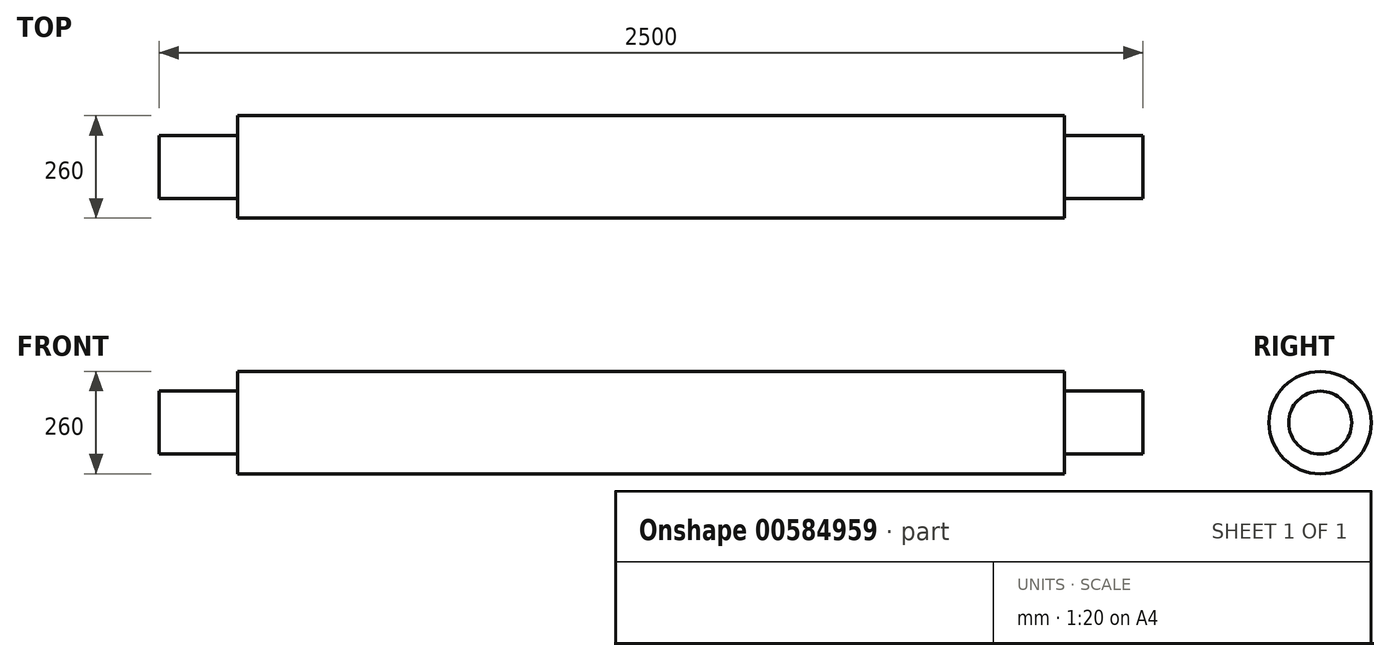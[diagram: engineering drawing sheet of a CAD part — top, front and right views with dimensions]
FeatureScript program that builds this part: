
annotation { "Feature Type Name" : "Feature", "Feature Type Description" : "" }
export const myFeature = defineFeature(function(context is Context, id is Id, definition is map)
    precondition{}
    {
        {
            var Q0;
            Q0=qCreatedBy(makeId("Front.planeOp"),FACE);
            var sketch = newSketch(context, id + "F0", { "sketchPlane" : qUnion([Q0])});
            skLineSegment(sketch, "E0", {"start": v(-1250, 0) * mm, "end": v(1250, 0) * mm});
            skLineSegment(sketch, "E1", {"start": v(0, 130) * mm, "end": v(0, 0) * mm, "construction": true});
            skLineSegment(sketch, "E2", {"start": v(0, 0) * mm, "end": v(0, 0) * mm});
            skLineSegment(sketch, "E3", {"start": v(-1250, 0) * mm, "end": v(-1250, 80) * mm});
            skLineSegment(sketch, "E4", {"start": v(-1250, 80) * mm, "end": v(-1050, 80) * mm});
            skLineSegment(sketch, "E5", {"start": v(-1050, 80) * mm, "end": v(-1050, 130) * mm});
            skLineSegment(sketch, "E6", {"start": v(-1050, 130) * mm, "end": v(0, 130) * mm});
            skLineSegment(sketch, "E7.MirrorCS", {"start": v(1050, 80) * mm, "end": v(1050, 130) * mm});
            skLineSegment(sketch, "E8.MirrorCS", {"start": v(1250, 0) * mm, "end": v(1250, 80) * mm});
            skLineSegment(sketch, "E9.MirrorCS", {"start": v(1250, 80) * mm, "end": v(1050, 80) * mm});
            skLineSegment(sketch, "E10.MirrorCS", {"start": v(1050, 130) * mm, "end": v(0, 130) * mm});
            skSolve(sketch);
        }
        {
            var Q0;
            Q0=makeQuery(id+"F0.imprint","IMPRINT",FACE,{"disambiguationData":[TD([[makeQuery(id+"F0.imprint","IMPRINT",EDGE,{"derivedFrom":sQuery(id+"F0.wireOp",EDGE,"E0")}),1.0]])]});
            var Q1;
            Q1=sQuery(id+"F0.wireOp",EDGE,"E0");
            revolve(context, id + "F1", {"entities" : qUnion([Q0]), "axis" : qUnion([Q1]), "revolveType" : RevolveType.FULL});
        }
    });
